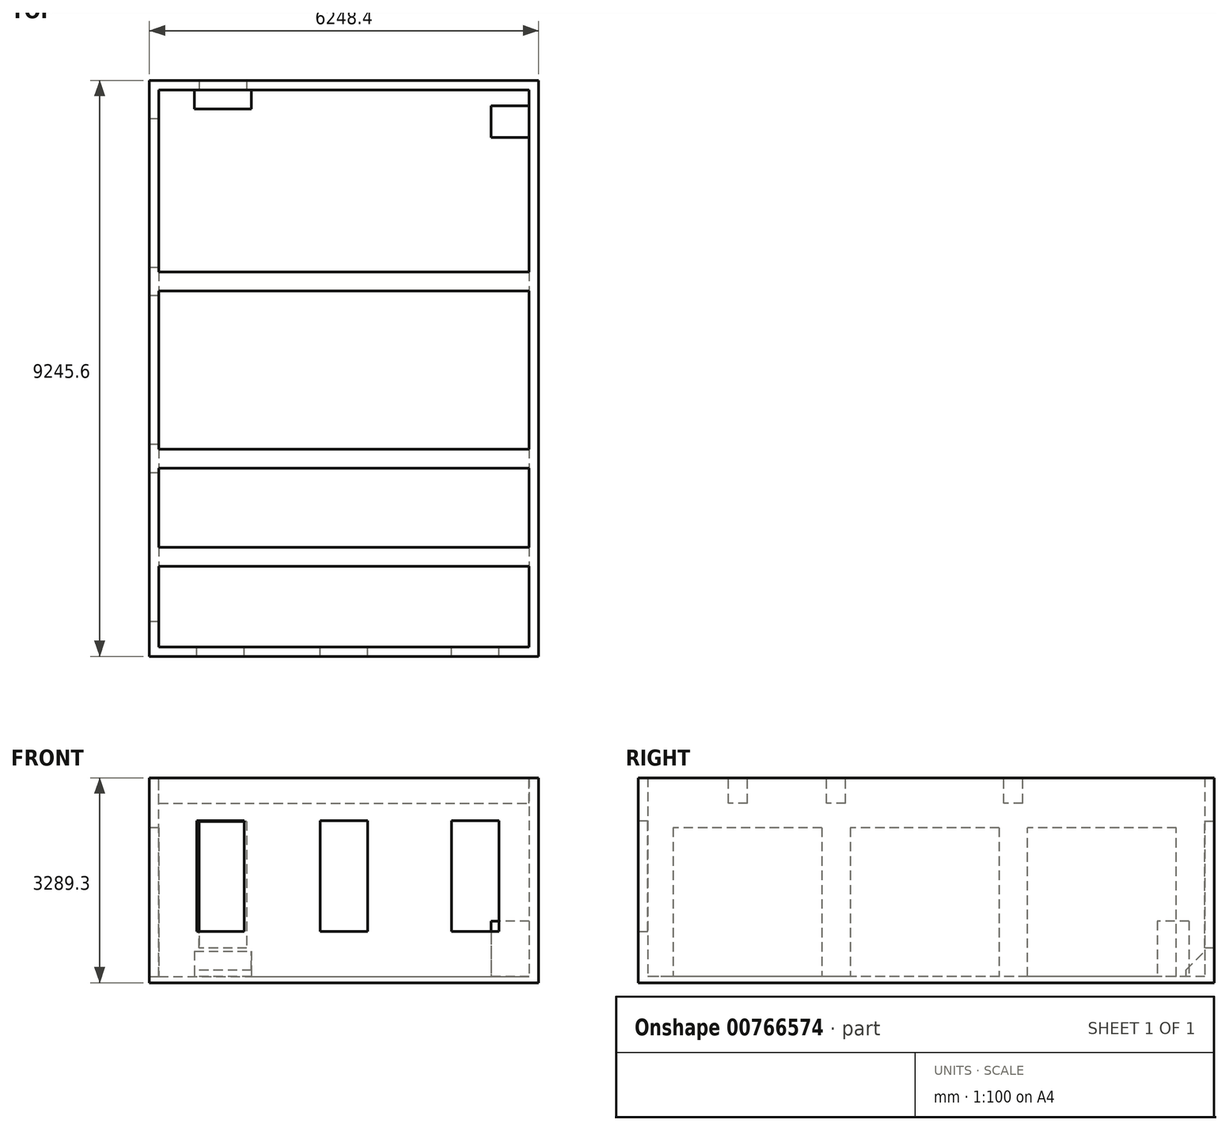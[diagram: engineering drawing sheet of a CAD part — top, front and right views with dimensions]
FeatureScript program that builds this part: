
annotation { "Feature Type Name" : "Feature", "Feature Type Description" : "" }
export const myFeature = defineFeature(function(context is Context, id is Id, definition is map)
    precondition{}
    {
        {
            var Q0;
            Q0=qCreatedBy(makeId("Top.planeOp"),FACE);
            var sketch = newSketch(context, id + "F0", { "sketchPlane" : qUnion([Q0])});
            skLineSegment(sketch, "E0.bottom", {"start": v(-3124.2, 4622.8) * mm, "end": v(3124.2, 4622.8) * mm});
            skLineSegment(sketch, "E0.top", {"start": v(-3124.2, -4622.8) * mm, "end": v(3124.2, -4622.8) * mm});
            skLineSegment(sketch, "E0.left", {"start": v(-3124.2, 4622.8) * mm, "end": v(-3124.2, -4622.8) * mm});
            skLineSegment(sketch, "E0.right", {"start": v(3124.2, 4622.8) * mm, "end": v(3124.2, -4622.8) * mm});
            skLineSegment(sketch, "E1", {"start": v(-3124.2, 4622.8) * mm, "end": v(3124.2, -4622.8) * mm, "construction": true});
            skSolve(sketch);
        }
        {
            var Q0;
            Q0 = qSketchRegion(id + "F0", true);
            var Q1;
            Q1=sQuery(id+"F0.wireOp",EDGE,"E0.left");
            var Q2;
            Q2=sQuery(id+"F0.wireOp",EDGE,"E0.bottom");
            var Q3;
            Q3=sQuery(id+"F0.wireOp",EDGE,"E0.right");
            var Q4;
            Q4=sQuery(id+"F0.wireOp",EDGE,"E0.top");
            extrude(context, id + "F1", {"entities" : qUnion([Q0]), "surfaceOperationType" : NewSurfaceOperationType.ADD, "surfaceEntities" : qUnion([Q1, Q2, Q3, Q4]), "depth" : 3340.1 * mm, "offsetDistance" : 25.4 * mm, "hasSecondDirection" : true, "secondDirectionOppositeDirection" : true, "secondDirectionDepth" : 101.6 * mm});
        }
        {
            var Q0;
            Q0=makeQuery(id+"F1.opExtrude","SWEPT_FACE",FACE,{"disambiguationData":[OSD([sQuery(id+"F0.wireOp",EDGE,"E0.left")])]});
            var sketch = newSketch(context, id + "F2", { "sketchPlane" : qUnion([Q0])});
            skLineSegment(sketch, "E2.bottom", {"start": v(-4013.2, 0) * mm, "end": v(-1625.6, 0) * mm});
            skLineSegment(sketch, "E2.top", {"start": v(-4013.2, 2387.6) * mm, "end": v(-1625.6, 2387.6) * mm});
            skLineSegment(sketch, "E2.left", {"start": v(-4013.2, 0) * mm, "end": v(-4013.2, 2387.6) * mm});
            skLineSegment(sketch, "E2.right", {"start": v(-1625.6, 0) * mm, "end": v(-1625.6, 2387.6) * mm});
            skLineSegment(sketch, "E3.bottom", {"start": v(-1168.4, 2387.6) * mm, "end": v(1219.2, 2387.6) * mm});
            skLineSegment(sketch, "E3.top", {"start": v(-1168.4, 0) * mm, "end": v(1219.2, 0) * mm});
            skLineSegment(sketch, "E3.left", {"start": v(-1168.4, 2387.6) * mm, "end": v(-1168.4, 0) * mm});
            skLineSegment(sketch, "E3.right", {"start": v(1219.2, 2387.6) * mm, "end": v(1219.2, 0) * mm});
            skLineSegment(sketch, "E4.bottom", {"start": v(1676.4, 2387.6) * mm, "end": v(4064, 2387.6) * mm});
            skLineSegment(sketch, "E4.top", {"start": v(1676.4, 0) * mm, "end": v(4064, 0) * mm});
            skLineSegment(sketch, "E4.left", {"start": v(1676.4, 2387.6) * mm, "end": v(1676.4, 0) * mm});
            skLineSegment(sketch, "E4.right", {"start": v(4064, 2387.6) * mm, "end": v(4064, 0) * mm});
            skSolve(sketch);
        }
        {
            var Q0;
            Q0=makeQuery(id+"F1.opExtrude","SWEPT_FACE",FACE,{"disambiguationData":[OSD([sQuery(id+"F0.wireOp",EDGE,"E0.left")])]});
            shell(context, id + "F3", {"entities" : qUnion([Q0]), "thickness" : 152.4 * mm});
        }
        {
            var Q0;
            Q0=makeQuery(id+"F2.imprint","IMPRINT",FACE,{"disambiguationData":[TD([[makeQuery(id+"F2.imprint","IMPRINT",EDGE,{"derivedFrom":sQuery(id+"F2.wireOp",EDGE,"E2.bottom")}),-1.0]])]});
            extrude(context, id + "F4", {"entities" : qUnion([Q0]), "operationType" : NewBodyOperationType.ADD, "oppositeDirection" : true, "depth" : 152.4 * mm, "offsetDistance" : 25.4 * mm});
        }
        {
            var Q0;
            {var subQ0=sQuery(id+"F0.wireOp",EDGE,"E0.right");var subQ1=sQuery(id+"F0.wireOp",EDGE,"E0.left");var subQ2=sQuery(id+"F0.wireOp",EDGE,"E0.top");var subQ3=sQuery(id+"F0.wireOp",EDGE,"E0.bottom");Q0=makeQuery(id+"F3.opShell","OFFSET_FACE",FACE,{"disambiguationData":[OSD([subQ3,subQ2,subQ1,subQ0]),TDD([makeQuery(id+"F1.opExtrude","CAP_FACE",FACE,{"disambiguationData":[OSD([subQ3,subQ2,subQ1,subQ0])],"isStart":true})])]});}
            extrude(context, id + "F5", {"entities" : qUnion([Q0]), "operationType" : NewBodyOperationType.REMOVE, "oppositeDirection" : true, "depth" : 50.8 * mm, "offsetDistance" : 25.4 * mm});
        }
        {
            var Q0;
            Q0=makeQuery(id+"F5.boolean.opBoolean","COPY",FACE,{"derivedFrom":makeQuery(id+"F5.opExtrude","CAP_FACE",FACE,{"disambiguationData":[OSD([sQuery(id+"F0.wireOp",EDGE,"E0.bottom"),sQuery(id+"F0.wireOp",EDGE,"E0.top"),sQuery(id+"F0.wireOp",EDGE,"E0.left"),sQuery(id+"F0.wireOp",EDGE,"E0.right")])],"isStart":false})});
            var sketch = newSketch(context, id + "F6", { "sketchPlane" : qUnion([Q0])});
            skLineSegment(sketch, "E5.bottom", {"start": v(-1485.9, 4470.4) * mm, "end": v(-2400.3, 4470.4) * mm});
            skLineSegment(sketch, "E5.top", {"start": v(-1485.9, 4165.6) * mm, "end": v(-2400.3, 4165.6) * mm});
            skLineSegment(sketch, "E5.left", {"start": v(-1485.9, 4470.4) * mm, "end": v(-1485.9, 4165.6) * mm});
            skLineSegment(sketch, "E5.right", {"start": v(-2400.3, 4470.4) * mm, "end": v(-2400.3, 4165.6) * mm});
            skSolve(sketch);
        }
        {
            var Q0;
            Q0 = qSketchRegion(id + "F6", true);
            extrude(context, id + "F7", {"entities" : qUnion([Q0]), "operationType" : NewBodyOperationType.ADD, "depth" : 406.4 * mm, "offsetDistance" : 25.4 * mm});
        }
        {
            var Q0;
            Q0=makeQuery(id+"F7.opExtrude","CAP_EDGE",EDGE,{"disambiguationData":[OSD([sQuery(id+"F6.wireOp",EDGE,"E5.top")])],"isStart":false});
            chamfer(context, id + "F8", {"entities" : qUnion([Q0]), "width" : 304.8 * mm, "tangentPropagation" : true});
        }
        {
            var Q0;
            {var subQ0=sQuery(id+"F0.wireOp",EDGE,"E0.right");var subQ1=sQuery(id+"F0.wireOp",EDGE,"E0.left");var subQ2=sQuery(id+"F0.wireOp",EDGE,"E0.top");var subQ3=sQuery(id+"F0.wireOp",EDGE,"E0.bottom");Q0=makeQuery(id+"F3.opShell","OFFSET_FACE",FACE,{"disambiguationData":[OSD([subQ3,subQ2,subQ1,subQ0]),TDD([makeQuery(id+"F1.opExtrude","CAP_FACE",FACE,{"disambiguationData":[OSD([subQ3,subQ2,subQ1,subQ0])],"isStart":false})])]});}
            var sketch = newSketch(context, id + "F9", { "sketchPlane" : qUnion([Q0])});
            skLineSegment(sketch, "E6.bottom", {"start": v(-2971.8, 1295.4) * mm, "end": v(2971.8, 1295.4) * mm});
            skLineSegment(sketch, "E6.top", {"start": v(-2971.8, 1600.2) * mm, "end": v(2971.8, 1600.2) * mm});
            skLineSegment(sketch, "E6.left", {"start": v(-2971.8, 1295.4) * mm, "end": v(-2971.8, 1600.2) * mm});
            skLineSegment(sketch, "E6.right", {"start": v(2971.8, 1295.4) * mm, "end": v(2971.8, 1600.2) * mm});
            skLineSegment(sketch, "E7.bottom", {"start": v(-2971.8, -1549.4) * mm, "end": v(2971.8, -1549.4) * mm});
            skLineSegment(sketch, "E7.top", {"start": v(-2971.8, -1244.6) * mm, "end": v(2971.8, -1244.6) * mm});
            skLineSegment(sketch, "E7.left", {"start": v(-2971.8, -1549.4) * mm, "end": v(-2971.8, -1244.6) * mm});
            skLineSegment(sketch, "E7.right", {"start": v(2971.8, -1549.4) * mm, "end": v(2971.8, -1244.6) * mm});
            skLineSegment(sketch, "E8.bottom", {"start": v(-2971.8, 2870.2) * mm, "end": v(2971.8, 2870.2) * mm});
            skLineSegment(sketch, "E8.top", {"start": v(-2971.8, 3175) * mm, "end": v(2971.8, 3175) * mm});
            skLineSegment(sketch, "E8.left", {"start": v(-2971.8, 2870.2) * mm, "end": v(-2971.8, 3175) * mm});
            skLineSegment(sketch, "E8.right", {"start": v(2971.8, 2870.2) * mm, "end": v(2971.8, 3175) * mm});
            skSolve(sketch);
        }
        {
            var Q0;
            Q0 = qSketchRegion(id + "F9", true);
            extrude(context, id + "F10", {"entities" : qUnion([Q0]), "operationType" : NewBodyOperationType.ADD, "depth" : 406.4 * mm, "offsetDistance" : 25.4 * mm});
        }
        {
            var Q0;
            {var subQ0=sQuery(id+"F0.wireOp",EDGE,"E0.top");Q0=makeQuery(id+"F5.boolean.opBoolean","MERGE",FACE,{"derivedFrom":[makeQuery(id+"F3.opShell","OFFSET_FACE",FACE,{"disambiguationData":[OSD([subQ0])]}),makeQuery(id+"F5.opExtrude","SWEPT_FACE",FACE,{"disambiguationData":[OSD([subQ0])]})]});}
            var sketch = newSketch(context, id + "F11", { "sketchPlane" : qUnion([Q0])});
            skLineSegment(sketch, "E9.bottom", {"start": v(1600.2, 723.9) * mm, "end": v(2362.2, 723.9) * mm});
            skLineSegment(sketch, "E9.top", {"start": v(1600.2, 2501.9) * mm, "end": v(2362.2, 2501.9) * mm});
            skLineSegment(sketch, "E9.left", {"start": v(1600.2, 723.9) * mm, "end": v(1600.2, 2501.9) * mm});
            skLineSegment(sketch, "E9.right", {"start": v(2362.2, 723.9) * mm, "end": v(2362.2, 2501.9) * mm});
            skLineSegment(sketch, "E10.bottom", {"start": v(-381, 723.9) * mm, "end": v(381, 723.9) * mm});
            skLineSegment(sketch, "E10.top", {"start": v(-381, 2501.9) * mm, "end": v(381, 2501.9) * mm});
            skLineSegment(sketch, "E10.left", {"start": v(-381, 723.9) * mm, "end": v(-381, 2501.9) * mm});
            skLineSegment(sketch, "E10.right", {"start": v(381, 723.9) * mm, "end": v(381, 2501.9) * mm});
            skLineSegment(sketch, "E11.bottom", {"start": v(-2489.2, 723.9) * mm, "end": v(-1727.2, 723.9) * mm});
            skLineSegment(sketch, "E11.top", {"start": v(-2489.2, 2501.9) * mm, "end": v(-1727.2, 2501.9) * mm});
            skLineSegment(sketch, "E11.left", {"start": v(-2489.2, 723.9) * mm, "end": v(-2489.2, 2501.9) * mm});
            skLineSegment(sketch, "E11.right", {"start": v(-1727.2, 723.9) * mm, "end": v(-1727.2, 2501.9) * mm});
            skSolve(sketch);
        }
        {
            var Q0;
            Q0 = qSketchRegion(id + "F11", true);
            extrude(context, id + "F12", {"entities" : qUnion([Q0]), "operationType" : NewBodyOperationType.REMOVE, "endBound" : BoundingType.THROUGH_ALL, "oppositeDirection" : true, "depth" : 25.4 * mm, "offsetDistance" : 25.4 * mm});
        }
        {
            var Q0;
            Q0=makeQuery(id+"F5.boolean.opBoolean","COPY",FACE,{"derivedFrom":makeQuery(id+"F5.opExtrude","CAP_FACE",FACE,{"disambiguationData":[OSD([sQuery(id+"F0.wireOp",EDGE,"E0.bottom"),sQuery(id+"F0.wireOp",EDGE,"E0.top"),sQuery(id+"F0.wireOp",EDGE,"E0.left"),sQuery(id+"F0.wireOp",EDGE,"E0.right")])],"isStart":false})});
            var sketch = newSketch(context, id + "F13", { "sketchPlane" : qUnion([Q0])});
            skLineSegment(sketch, "E12.bottom", {"start": v(2971.8, 4216.4) * mm, "end": v(2362.2, 4216.4) * mm});
            skLineSegment(sketch, "E12.top", {"start": v(2971.8, 3708.4) * mm, "end": v(2362.2, 3708.4) * mm});
            skLineSegment(sketch, "E12.left", {"start": v(2971.8, 4216.4) * mm, "end": v(2971.8, 3708.4) * mm});
            skLineSegment(sketch, "E12.right", {"start": v(2362.2, 4216.4) * mm, "end": v(2362.2, 3708.4) * mm});
            skSolve(sketch);
        }
        {
            var Q0;
            Q0 = qSketchRegion(id + "F13", true);
            extrude(context, id + "F14", {"entities" : qUnion([Q0]), "operationType" : NewBodyOperationType.ADD, "depth" : 889 * mm, "offsetDistance" : 25.4 * mm});
        }
        {
            var Q0;
            {var subQ0=sQuery(id+"F0.wireOp",EDGE,"E0.bottom");Q0=makeQuery(id+"F5.boolean.opBoolean","MERGE",FACE,{"derivedFrom":[makeQuery(id+"F3.opShell","OFFSET_FACE",FACE,{"disambiguationData":[OSD([subQ0])]}),makeQuery(id+"F5.opExtrude","SWEPT_FACE",FACE,{"disambiguationData":[OSD([subQ0])]})]});}
            var sketch = newSketch(context, id + "F15", { "sketchPlane" : qUnion([Q0])});
            skLineSegment(sketch, "E13.bottom", {"start": v(-2324.1, 457.2) * mm, "end": v(-1562.1, 457.2) * mm});
            skLineSegment(sketch, "E13.top", {"start": v(-2324.1, 2489.2) * mm, "end": v(-1562.1, 2489.2) * mm});
            skLineSegment(sketch, "E13.left", {"start": v(-2324.1, 457.2) * mm, "end": v(-2324.1, 2489.2) * mm});
            skLineSegment(sketch, "E13.right", {"start": v(-1562.1, 457.2) * mm, "end": v(-1562.1, 2489.2) * mm});
            skLineSegment(sketch, "E14", {"start": v(-1943.1, 406.4) * mm, "end": v(-1943.1, 457.2) * mm, "construction": true});
            skSolve(sketch);
        }
        {
            var Q0;
            Q0 = qSketchRegion(id + "F15", true);
            extrude(context, id + "F16", {"entities" : qUnion([Q0]), "operationType" : NewBodyOperationType.REMOVE, "endBound" : BoundingType.THROUGH_ALL, "oppositeDirection" : true, "depth" : 25.4 * mm, "offsetDistance" : 25.4 * mm});
        }
        {
            var Q0;
            Q0=makeQuery(id+"F1.opExtrude","CAP_FACE",FACE,{"disambiguationData":[OSD([sQuery(id+"F0.wireOp",EDGE,"E0.bottom"),sQuery(id+"F0.wireOp",EDGE,"E0.top"),sQuery(id+"F0.wireOp",EDGE,"E0.left"),sQuery(id+"F0.wireOp",EDGE,"E0.right")])],"isStart":false});
            extrude(context, id + "F17", {"entities" : qUnion([Q0]), "operationType" : NewBodyOperationType.REMOVE, "oppositeDirection" : true, "depth" : 152.4 * mm, "offsetDistance" : 25.4 * mm});
        }
    });
